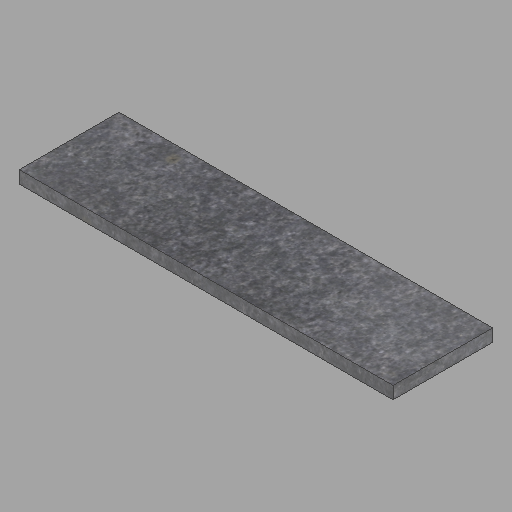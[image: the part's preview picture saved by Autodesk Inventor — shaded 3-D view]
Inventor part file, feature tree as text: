
AUTODESK INVENTOR PART (.ipt)
format: ipt  version: 2023 (Build 270158000, 158)  size: 192,512 bytes
history: native  units: in
note: dims shown in document units (in); Inventor stores cm internally (conversion verified against a paired STEP export)
features: other x1, extrude x1, sketch x1
ambient origin geometry x8: Origin, YZ Plane, XZ Plane, XY Plane, X Axis, Y Axis, Z Axis, Center Point
bodies: Solid1 (feature_tree)
feature tree (3):
  other  "2x16x60-6"
  extrude  "Extrusion1"  Depth=16.0in
  sketch  "Sketch1"  dims[d0=2.0in d1=16.0in d2=60.0in d3=0.0in]
